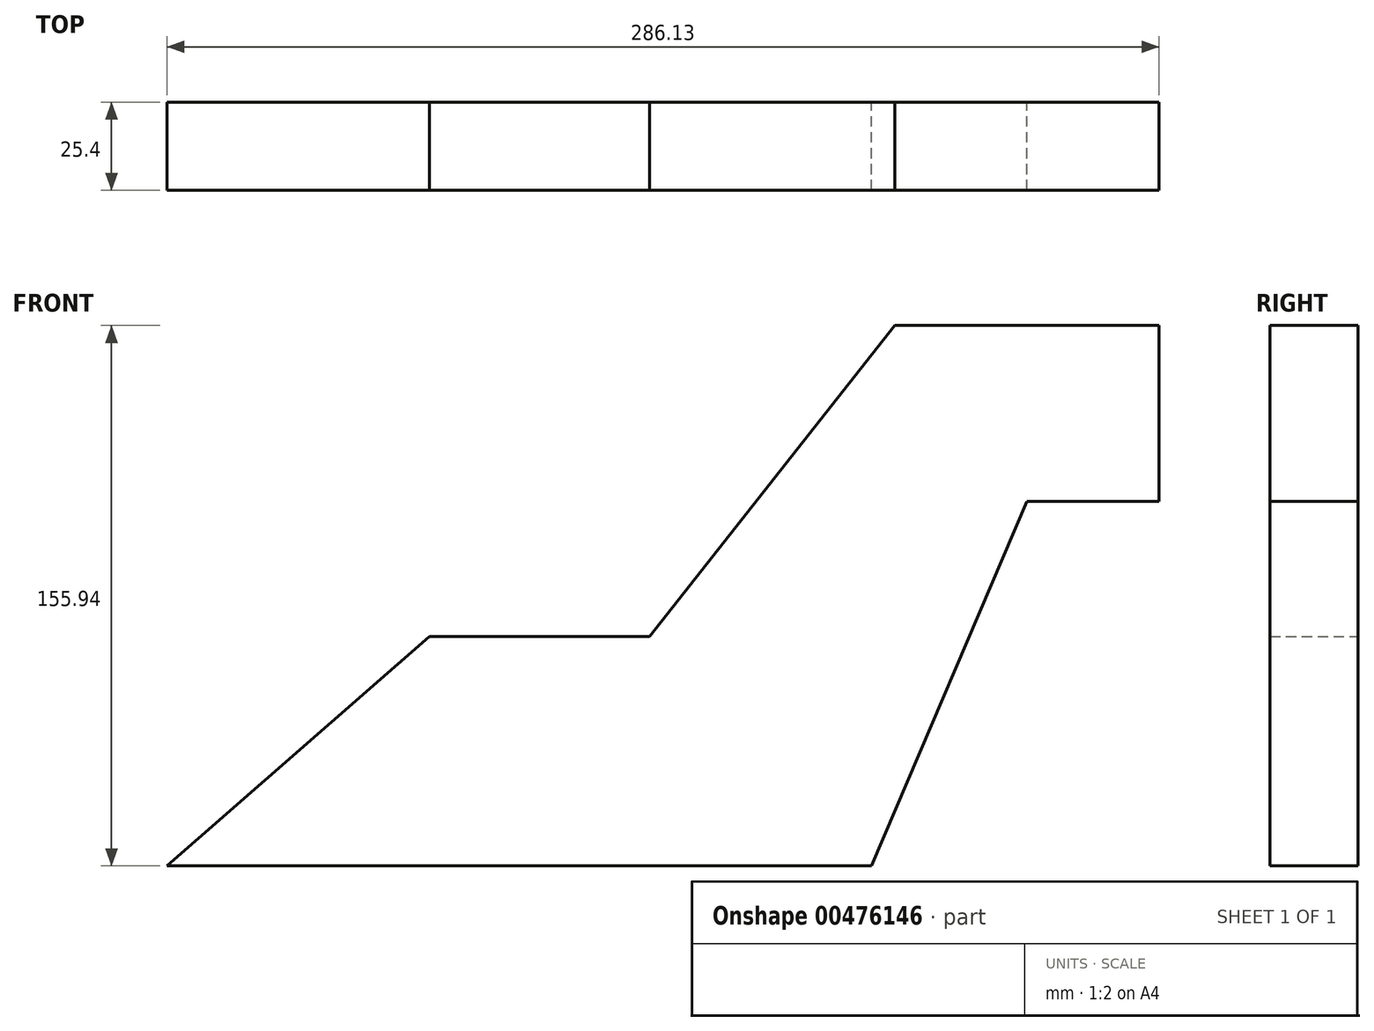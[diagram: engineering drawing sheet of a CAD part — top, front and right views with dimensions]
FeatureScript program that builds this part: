
annotation { "Feature Type Name" : "Feature", "Feature Type Description" : "" }
export const myFeature = defineFeature(function(context is Context, id is Id, definition is map)
    precondition{}
    {
        {
            var Q0;
            Q0=qCreatedBy(makeId("Front.planeOp"),FACE);
            var sketch = newSketch(context, id + "F0", { "sketchPlane" : qUnion([Q0])});
            skLineSegment(sketch, "E0", {"start": v(-139.68, 0) * mm, "end": v(-64, 66.16) * mm});
            skLineSegment(sketch, "E1", {"start": v(-64, 66.16) * mm, "end": v(-0.5, 66.16) * mm});
            skLineSegment(sketch, "E2", {"start": v(-0.5, 66.16) * mm, "end": v(70.25, 155.94) * mm});
            skLineSegment(sketch, "E3", {"start": v(70.25, 155.94) * mm, "end": v(146.45, 155.94) * mm});
            skLineSegment(sketch, "E4", {"start": v(146.45, 155.94) * mm, "end": v(146.45, 105.14) * mm});
            skLineSegment(sketch, "E5", {"start": v(146.45, 105.14) * mm, "end": v(108.35, 105.14) * mm});
            skLineSegment(sketch, "E6", {"start": v(108.35, 105.14) * mm, "end": v(63.52, 0) * mm});
            skLineSegment(sketch, "E7", {"start": v(63.52, 0) * mm, "end": v(-139.68, 0) * mm});
            skSolve(sketch);
        }
        {
            var Q0;
            Q0=makeQuery(id+"F0.imprint","IMPRINT",FACE,{"disambiguationData":[TD([[makeQuery(id+"F0.imprint","IMPRINT",EDGE,{"derivedFrom":sQuery(id+"F0.wireOp",EDGE,"E0")}),-1.0]])]});
            extrude(context, id + "F1", {"entities" : qUnion([Q0]), "depth" : 25.4 * mm});
        }
    });
